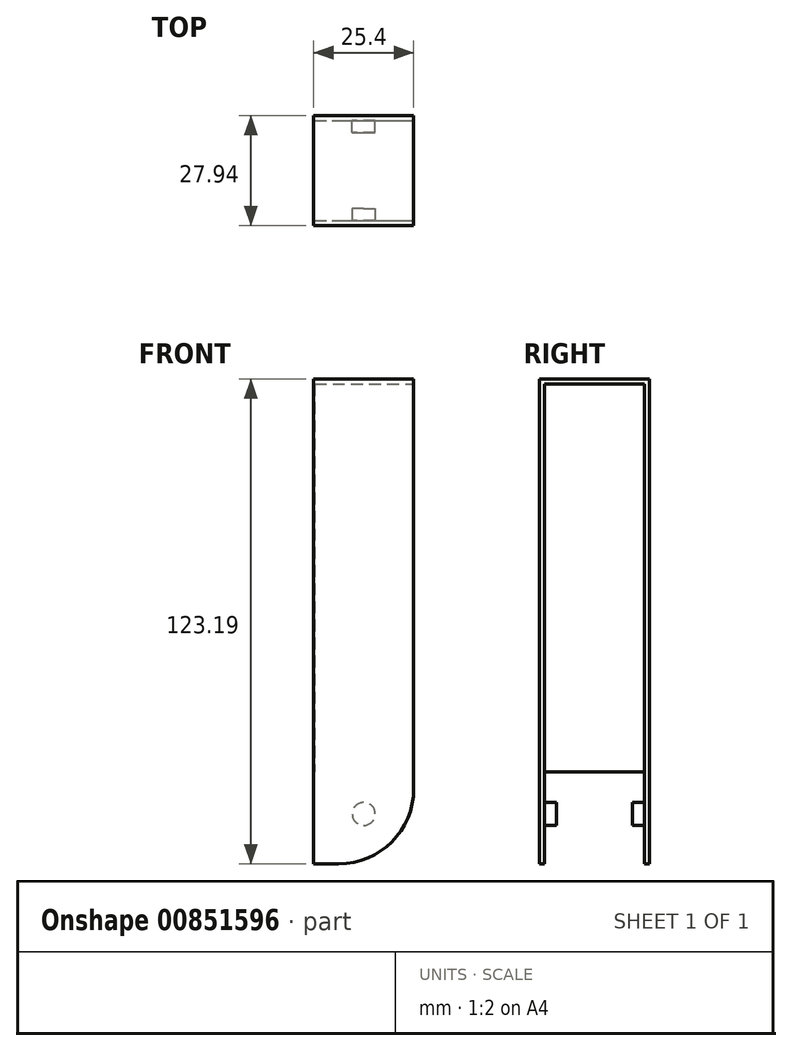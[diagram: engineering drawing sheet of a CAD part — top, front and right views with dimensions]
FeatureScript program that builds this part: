
annotation { "Feature Type Name" : "Feature", "Feature Type Description" : "" }
export const myFeature = defineFeature(function(context is Context, id is Id, definition is map)
    precondition{}
    {
        {
            var Q0;
            Q0=qCreatedBy(makeId("Front.planeOp"),FACE);
            var sketch = newSketch(context, id + "F0", { "sketchPlane" : qUnion([Q0])});
            skLineSegment(sketch, "E0.bottom", {"start": v(-25.4, 123.2) * mm, "end": v(0, 123.2) * mm});
            skLineSegment(sketch, "E0.top", {"start": v(-25.4, 0) * mm, "end": v(-19.05, 0) * mm});
            skLineSegment(sketch, "E0.left", {"start": v(-25.4, 123.2) * mm, "end": v(-25.4, 0) * mm});
            skLineSegment(sketch, "E0.right", {"start": v(0, 123.2) * mm, "end": v(0, 19.05) * mm});
            skPoint(sketch, "E1.visualSharp", {"position": v(0, 0) * mm});
            skArc(sketch, "E1.filletArc", {"start": v(-19.05, 0) * mm, "mid": v(-5.58, 5.58) * mm, "end": v(0, 19.05) * mm});
            skSolve(sketch);
        }
        {
            var Q0;
            Q0 = qSketchRegion(id + "F0", true);
            extrude(context, id + "F1", {"entities" : qUnion([Q0]), "depth" : 27.94 * mm, "offsetDistance" : 25.4 * mm});
        }
        {
            var Q0;
            Q0=makeQuery(id+"F1.opExtrude","SWEPT_FACE",FACE,{"disambiguationData":[OSD([sQuery(id+"F0.wireOp",EDGE,"E0.right")])]});
            var sketch = newSketch(context, id + "F2", { "sketchPlane" : qUnion([Q0])});
            skLineSegment(sketch, "E2.0", {"start": v(-1.27, 20.32) * mm, "end": v(-1.27, 121.92) * mm});
            skLineSegment(sketch, "E2.2", {"start": v(-26.67, 121.92) * mm, "end": v(-26.67, 20.32) * mm});
            skLineSegment(sketch, "E2.3", {"start": v(-1.27, 121.92) * mm, "end": v(-26.67, 121.92) * mm});
            skLineSegment(sketch, "E3", {"start": v(-26.67, 20.32) * mm, "end": v(-26.67, -8.35) * mm});
            skLineSegment(sketch, "E4", {"start": v(-1.27, 20.32) * mm, "end": v(-1.27, -9.12) * mm});
            skLineSegment(sketch, "E5", {"start": v(-26.67, -8.35) * mm, "end": v(-1.27, -9.12) * mm});
            skSolve(sketch);
        }
        {
            var Q0;
            {var subQ0=sQuery(id+"F2.wireOp",EDGE,"E5");Q0=makeQuery(id+"F2.imprint","IMPRINT",FACE,{"disambiguationData":[TD([[makeQuery(id+"F2.imprint","IMPRINT",EDGE,{"derivedFrom":subQ0}),1.0]])]});}
            var Q1;
            {var subQ6=sQuery(id+"F2.wireOp",EDGE,"E2.0");Q1=makeQuery(id+"F2.imprint","IMPRINT",FACE,{"disambiguationData":[TD([[makeQuery(id+"F2.imprint","IMPRINT",EDGE,{"derivedFrom":subQ6}),1.0]])]});}
            extrude(context, id + "F3", {"entities" : qUnion([Q0, Q1]), "operationType" : NewBodyOperationType.REMOVE, "oppositeDirection" : true, "depth" : 25.15 * mm, "offsetDistance" : 25.4 * mm});
        }
        {
            var Q0;
            Q0=makeQuery(id+"F3.boolean.opBoolean","COPY",FACE,{"derivedFrom":makeQuery(id+"F3.opExtrude","SWEPT_FACE",FACE,{"disambiguationData":[OSD([sQuery(id+"F2.wireOp",EDGE,"E2.2"),sQuery(id+"F2.wireOp",EDGE,"E3")])]})});
            var sketch = newSketch(context, id + "F4", { "sketchPlane" : qUnion([Q0])});
            skCircle(sketch, "E6", {"center": v(12.7, 12.7) * mm, "radius": 2.92 * mm});
            skSolve(sketch);
        }
        {
            var Q0;
            Q0=makeQuery(id+"F3.boolean.opBoolean","COPY",FACE,{"derivedFrom":makeQuery(id+"F3.opExtrude","SWEPT_FACE",FACE,{"disambiguationData":[OSD([sQuery(id+"F2.wireOp",EDGE,"E2.0"),sQuery(id+"F2.wireOp",EDGE,"E4")])]})});
            var sketch = newSketch(context, id + "F5", { "sketchPlane" : qUnion([Q0])});
            skCircle(sketch, "E7", {"center": v(-12.7, 12.7) * mm, "radius": 2.92 * mm});
            skSolve(sketch);
        }
        {
            var Q0;
            Q0=makeQuery(id+"F4.imprint","IMPRINT",FACE,{"disambiguationData":[TD([[makeQuery(id+"F4.imprint","IMPRINT",EDGE,{"derivedFrom":sQuery(id+"F4.wireOp",EDGE,"E6")}),1.0]])]});
            extrude(context, id + "F6", {"entities" : qUnion([Q0]), "operationType" : NewBodyOperationType.ADD, "depth" : 3.05 * mm, "offsetDistance" : 25.4 * mm});
        }
        {
            var Q0;
            Q0=makeQuery(id+"F5.imprint","IMPRINT",FACE,{"disambiguationData":[TD([[makeQuery(id+"F5.imprint","IMPRINT",EDGE,{"derivedFrom":sQuery(id+"F5.wireOp",EDGE,"E7")}),1.0]])]});
            extrude(context, id + "F7", {"entities" : qUnion([Q0]), "operationType" : NewBodyOperationType.ADD, "depth" : 3.05 * mm, "offsetDistance" : 25.4 * mm});
        }
        {
            var Q0;
            Q0=makeQuery(id+"F1.opExtrude","SWEPT_FACE",FACE,{"disambiguationData":[OSD([sQuery(id+"F0.wireOp",EDGE,"E0.left")])]});
            var sketch = newSketch(context, id + "F8", { "sketchPlane" : qUnion([Q0])});
            skLineSegment(sketch, "E8.0", {"start": v(1.27, 23.32) * mm, "end": v(1.27, 0.25) * mm});
            skLineSegment(sketch, "E8.2", {"start": v(26.67, 0.25) * mm, "end": v(26.67, 23.32) * mm});
            skLineSegment(sketch, "E9", {"start": v(1.27, 0.25) * mm, "end": v(1.27, -5.9) * mm});
            skLineSegment(sketch, "E10", {"start": v(26.67, 0.25) * mm, "end": v(26.67, -6.72) * mm});
            skLineSegment(sketch, "E11", {"start": v(26.67, -6.72) * mm, "end": v(1.27, -5.9) * mm});
            skLineSegment(sketch, "E12", {"start": v(1.27, 23.32) * mm, "end": v(26.67, 23.32) * mm});
            skSolve(sketch);
        }
        {
            var Q0;
            {var subQ5=sQuery(id+"F8.wireOp",EDGE,"E8.0");Q0=makeQuery(id+"F8.imprint","IMPRINT",FACE,{"disambiguationData":[TD([[makeQuery(id+"F8.imprint","IMPRINT",EDGE,{"derivedFrom":subQ5}),1.0]])]});}
            extrude(context, id + "F9", {"entities" : qUnion([Q0]), "operationType" : NewBodyOperationType.REMOVE, "oppositeDirection" : true, "depth" : 5.08 * mm, "offsetDistance" : 25.4 * mm});
        }
    });
